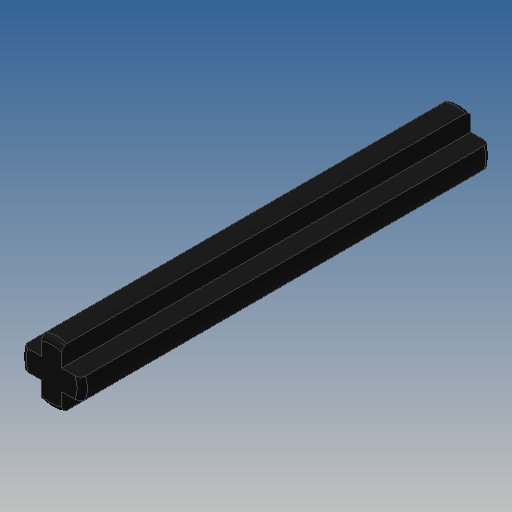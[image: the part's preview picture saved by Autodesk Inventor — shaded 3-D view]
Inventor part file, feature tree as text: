
AUTODESK INVENTOR PART (.ipt)
format: ipt  version: 2022.2 (Build 262287000, 287)  size: 147,968 bytes
history: native  units: in
note: dims shown in document units (in); Inventor stores cm internally (conversion verified against a paired STEP export)
features: extrude x1, fillet x1, sketch x1
ambient origin geometry x8: Origin, YZ Plane, XZ Plane, XY Plane, X Axis, Y Axis, Z Axis, Center Point
bodies: Solid1 (feature_tree)
feature tree (3):
  extrude  "Extrusion1"  Depth=0.0157in
  fillet  "Fillet1"  Radius=1.2598in
  sketch  "Sketch1"  dims[d0=0.189in d1=0.063in d2=1.2598in d3=0.0in d4=0.0157in d5=0.0in d6=0.0in]
